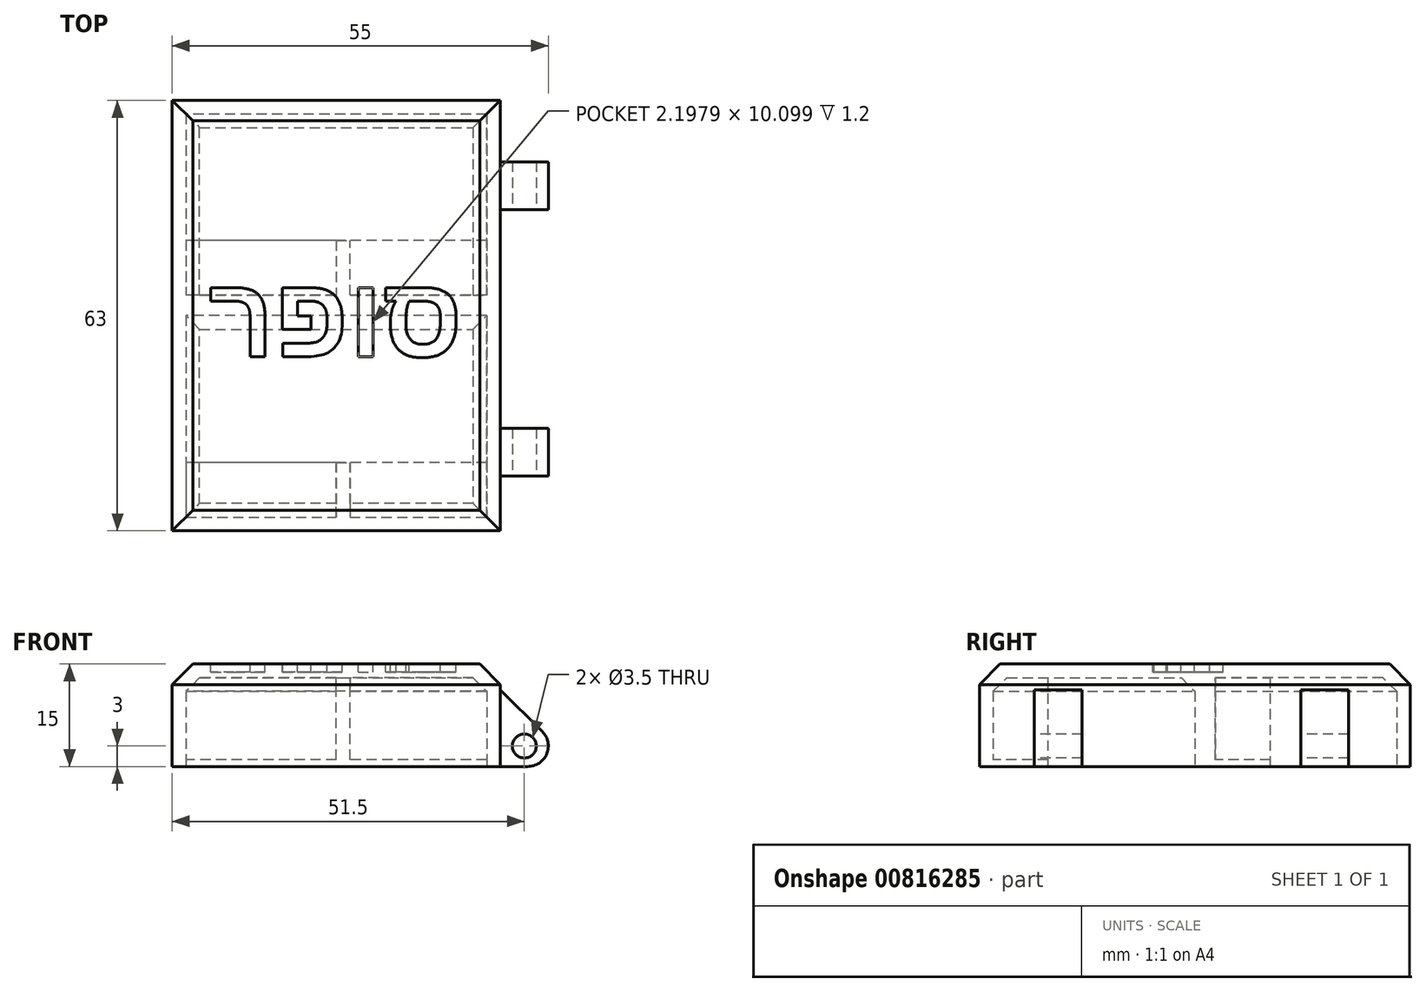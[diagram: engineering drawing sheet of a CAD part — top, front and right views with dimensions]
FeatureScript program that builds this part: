
annotation { "Feature Type Name" : "Feature", "Feature Type Description" : "" }
export const myFeature = defineFeature(function(context is Context, id is Id, definition is map)
    precondition{}
    {
        {
            var Q0;
            Q0=qCreatedBy(makeId("Top.planeOp"),FACE);
            var sketch = newSketch(context, id + "F0", { "sketchPlane" : qUnion([Q0])});
            skLineSegment(sketch, "E0.bottom", {"start": v(0, 0) * mm, "end": v(48, 0) * mm});
            skLineSegment(sketch, "E0.top", {"start": v(0, 63) * mm, "end": v(48, 63) * mm});
            skLineSegment(sketch, "E0.left", {"start": v(0, 0) * mm, "end": v(0, 63) * mm});
            skLineSegment(sketch, "E0.right", {"start": v(48, 0) * mm, "end": v(48, 63) * mm});
            skSolve(sketch);
        }
        {
            var Q0;
            Q0=makeQuery(id+"F0.imprint","IMPRINT",FACE,{"disambiguationData":[TD([[makeQuery(id+"F0.imprint","IMPRINT",EDGE,{"derivedFrom":sQuery(id+"F0.wireOp",EDGE,"E0.bottom")}),1.0]])]});
            extrude(context, id + "F1", {"entities" : qUnion([Q0]), "depth" : 15 * mm, "offsetDistance" : 25 * mm});
        }
        {
            var Q0;
            Q0=makeQuery(id+"F1.opExtrude","CAP_FACE",FACE,{"disambiguationData":[OSD([sQuery(id+"F0.wireOp",EDGE,"E0.bottom"),sQuery(id+"F0.wireOp",EDGE,"E0.top"),sQuery(id+"F0.wireOp",EDGE,"E0.left"),sQuery(id+"F0.wireOp",EDGE,"E0.right")])],"isStart":true});
            var sketch = newSketch(context, id + "F2", { "sketchPlane" : qUnion([Q0])});
            skLineSegment(sketch, "E1.bottom", {"start": v(46, -61) * mm, "end": v(2, -61) * mm});
            skLineSegment(sketch, "E1.top", {"start": v(46, -2) * mm, "end": v(2, -2) * mm});
            skLineSegment(sketch, "E1.left", {"start": v(46, -61) * mm, "end": v(46, -2) * mm});
            skLineSegment(sketch, "E1.right", {"start": v(2, -61) * mm, "end": v(2, -2) * mm});
            skSolve(sketch);
        }
        {
            var Q0;
            Q0 = qSketchRegion(id + "F2", true);
            extrude(context, id + "F3", {"entities" : qUnion([Q0]), "operationType" : NewBodyOperationType.REMOVE, "oppositeDirection" : true, "depth" : 13 * mm, "offsetDistance" : 25 * mm});
        }
        {
            var Q0;
            Q0=makeQuery(id+"F1.opExtrude","CAP_FACE",FACE,{"disambiguationData":[OSD([sQuery(id+"F0.wireOp",EDGE,"E0.bottom"),sQuery(id+"F0.wireOp",EDGE,"E0.top"),sQuery(id+"F0.wireOp",EDGE,"E0.left"),sQuery(id+"F0.wireOp",EDGE,"E0.right")])],"isStart":true});
            var sketch = newSketch(context, id + "F4", { "sketchPlane" : qUnion([Q0])});
            skLineSegment(sketch, "E2.bottom", {"start": v(48, -8) * mm, "end": v(55, -8) * mm});
            skLineSegment(sketch, "E2.top", {"start": v(48, -15) * mm, "end": v(55, -15) * mm});
            skLineSegment(sketch, "E2.left", {"start": v(48, -8) * mm, "end": v(48, -15) * mm});
            skLineSegment(sketch, "E2.right", {"start": v(55, -8) * mm, "end": v(55, -15) * mm});
            skLineSegment(sketch, "E3.bottom", {"start": v(48, -47) * mm, "end": v(55, -47) * mm});
            skLineSegment(sketch, "E3.top", {"start": v(48, -54) * mm, "end": v(55, -54) * mm});
            skLineSegment(sketch, "E3.left", {"start": v(48, -47) * mm, "end": v(48, -54) * mm});
            skLineSegment(sketch, "E3.right", {"start": v(55, -47) * mm, "end": v(55, -54) * mm});
            skSolve(sketch);
        }
        {
            var Q0;
            Q0=makeQuery(id+"F4.imprint","IMPRINT",FACE,{"disambiguationData":[TD([[makeQuery(id+"F4.imprint","IMPRINT",EDGE,{"derivedFrom":sQuery(id+"F4.wireOp",EDGE,"E2.bottom")}),-1.0]])]});
            var Q1;
            Q1=makeQuery(id+"F4.imprint","IMPRINT",FACE,{"disambiguationData":[TD([[makeQuery(id+"F4.imprint","IMPRINT",EDGE,{"derivedFrom":sQuery(id+"F4.wireOp",EDGE,"E3.bottom")}),-1.0]])]});
            extrude(context, id + "F5", {"entities" : qUnion([Q0, Q1]), "operationType" : NewBodyOperationType.ADD, "oppositeDirection" : true, "depth" : 6 * mm, "offsetDistance" : 25 * mm});
        }
        {
            var Q0;
            Q0=makeQuery(id+"F5.opExtrude","SWEPT_FACE",FACE,{"disambiguationData":[OSD([sQuery(id+"F4.wireOp",EDGE,"E2.bottom")])]});
            var sketch = newSketch(context, id + "F6", { "sketchPlane" : qUnion([Q0])});
            skLineSegment(sketch, "E4", {"start": v(48, 6) * mm, "end": v(55, 0) * mm, "construction": true});
            skCircle(sketch, "E5", {"center": v(51.5, 3) * mm, "radius": 1.75 * mm});
            skSolve(sketch);
        }
        {
            var Q0;
            Q0=makeQuery(id+"F6.imprint","IMPRINT",FACE,{"disambiguationData":[TD([[makeQuery(id+"F6.imprint","IMPRINT",EDGE,{"derivedFrom":sQuery(id+"F6.wireOp",EDGE,"E5")}),1.0]])]});
            extrude(context, id + "F7", {"entities" : qUnion([Q0]), "operationType" : NewBodyOperationType.REMOVE, "oppositeDirection" : true, "depth" : 60.8 * mm, "offsetDistance" : 25 * mm});
        }
        {
            var Q0;
            Q0=makeQuery(id+"F5.opExtrude","CAP_EDGE",EDGE,{"disambiguationData":[OSD([sQuery(id+"F4.wireOp",EDGE,"E2.right")])],"isStart":true});
            var Q1;
            Q1=makeQuery(id+"F5.opExtrude","CAP_EDGE",EDGE,{"disambiguationData":[OSD([sQuery(id+"F4.wireOp",EDGE,"E2.right")])],"isStart":false});
            var Q2;
            Q2=makeQuery(id+"F5.opExtrude","CAP_EDGE",EDGE,{"disambiguationData":[OSD([sQuery(id+"F4.wireOp",EDGE,"E3.right")])],"isStart":false});
            var Q3;
            Q3=makeQuery(id+"F5.opExtrude","CAP_EDGE",EDGE,{"disambiguationData":[OSD([sQuery(id+"F4.wireOp",EDGE,"E3.right")])],"isStart":true});
            fillet(context, id + "F8", {"entities" : qUnion([Q0, Q1, Q2, Q3]), "tangentPropagation" : true, "radius" : 3 * mm, "defaultsChanged" : false, "vertexSettings" : [], "allowEdgeOverflow" : false});
        }
        {
            var Q0;
            Q0=makeQuery(id+"F5.boolean.opBoolean","MERGE",FACE,{"derivedFrom":[makeQuery(id+"F1.opExtrude","CAP_FACE",FACE,{"disambiguationData":[OSD([sQuery(id+"F0.wireOp",EDGE,"E0.bottom"),sQuery(id+"F0.wireOp",EDGE,"E0.top"),sQuery(id+"F0.wireOp",EDGE,"E0.left"),sQuery(id+"F0.wireOp",EDGE,"E0.right")])],"isStart":true}),makeQuery(id+"F5.opExtrude","CAP_FACE",FACE,{"disambiguationData":[OSD([sQuery(id+"F4.wireOp",EDGE,"E2.bottom"),sQuery(id+"F4.wireOp",EDGE,"E2.top"),sQuery(id+"F4.wireOp",EDGE,"E2.left"),sQuery(id+"F4.wireOp",EDGE,"E2.right")])],"isStart":true}),makeQuery(id+"F5.opExtrude","CAP_FACE",FACE,{"disambiguationData":[OSD([sQuery(id+"F4.wireOp",EDGE,"E3.bottom"),sQuery(id+"F4.wireOp",EDGE,"E3.top"),sQuery(id+"F4.wireOp",EDGE,"E3.left"),sQuery(id+"F4.wireOp",EDGE,"E3.right")])],"isStart":true})]});
            var sketch = newSketch(context, id + "F9", { "sketchPlane" : qUnion([Q0])});
            skLineSegment(sketch, "E6.bottom", {"start": v(46, -34.5) * mm, "end": v(2, -34.5) * mm});
            skLineSegment(sketch, "E6.top", {"start": v(46, -31.5) * mm, "end": v(2, -31.5) * mm});
            skLineSegment(sketch, "E6.left", {"start": v(46, -34.5) * mm, "end": v(46, -31.5) * mm});
            skLineSegment(sketch, "E6.right", {"start": v(2, -34.5) * mm, "end": v(2, -31.5) * mm});
            skSolve(sketch);
        }
        {
            var Q0;
            Q0=makeQuery(id+"F9.imprint","IMPRINT",FACE,{"disambiguationData":[TD([[makeQuery(id+"F9.imprint","IMPRINT",EDGE,{"derivedFrom":sQuery(id+"F9.wireOp",EDGE,"E6.bottom")}),-1.0]])]});
            extrude(context, id + "F10", {"entities" : qUnion([Q0]), "operationType" : NewBodyOperationType.ADD, "endBound" : BoundingType.UP_TO_NEXT, "oppositeDirection" : true, "depth" : 25 * mm, "offsetDistance" : 25 * mm});
        }
        {
            var Q0;
            Q0=makeQuery(id+"F10.boolean.opBoolean","MERGE",FACE,{"derivedFrom":[makeQuery(id+"F5.boolean.opBoolean","MERGE",FACE,{"derivedFrom":[makeQuery(id+"F1.opExtrude","CAP_FACE",FACE,{"disambiguationData":[OSD([sQuery(id+"F0.wireOp",EDGE,"E0.bottom"),sQuery(id+"F0.wireOp",EDGE,"E0.top"),sQuery(id+"F0.wireOp",EDGE,"E0.left"),sQuery(id+"F0.wireOp",EDGE,"E0.right")])],"isStart":true}),makeQuery(id+"F5.opExtrude","CAP_FACE",FACE,{"disambiguationData":[OSD([sQuery(id+"F4.wireOp",EDGE,"E2.bottom"),sQuery(id+"F4.wireOp",EDGE,"E2.top"),sQuery(id+"F4.wireOp",EDGE,"E2.left"),sQuery(id+"F4.wireOp",EDGE,"E2.right")])],"isStart":true}),makeQuery(id+"F5.opExtrude","CAP_FACE",FACE,{"disambiguationData":[OSD([sQuery(id+"F4.wireOp",EDGE,"E3.bottom"),sQuery(id+"F4.wireOp",EDGE,"E3.top"),sQuery(id+"F4.wireOp",EDGE,"E3.left"),sQuery(id+"F4.wireOp",EDGE,"E3.right")])],"isStart":true})]}),makeQuery(id+"F10.opExtrude","CAP_FACE",FACE,{"disambiguationData":[OSD([sQuery(id+"F9.wireOp",EDGE,"E6.bottom"),sQuery(id+"F9.wireOp",EDGE,"E6.top"),sQuery(id+"F9.wireOp",EDGE,"E6.left"),sQuery(id+"F9.wireOp",EDGE,"E6.right")])],"isStart":true})]});
            var sketch = newSketch(context, id + "F11", { "sketchPlane" : qUnion([Q0])});
            skLineSegment(sketch, "E7.bottom", {"start": v(46, -34.5) * mm, "end": v(2, -34.5) * mm});
            skLineSegment(sketch, "E7.top", {"start": v(46, -42.5) * mm, "end": v(2, -42.5) * mm});
            skLineSegment(sketch, "E7.left", {"start": v(46, -34.5) * mm, "end": v(46, -42.5) * mm});
            skLineSegment(sketch, "E7.right", {"start": v(2, -34.5) * mm, "end": v(2, -42.5) * mm});
            skLineSegment(sketch, "E8.bottom", {"start": v(46, -2) * mm, "end": v(2, -2) * mm});
            skLineSegment(sketch, "E8.top", {"start": v(46, -10) * mm, "end": v(2, -10) * mm});
            skLineSegment(sketch, "E8.left", {"start": v(46, -2) * mm, "end": v(46, -10) * mm});
            skLineSegment(sketch, "E8.right", {"start": v(2, -2) * mm, "end": v(2, -10) * mm});
            skSolve(sketch);
        }
        {
            var Q0;
            Q0=makeQuery(id+"F11.imprint","IMPRINT",FACE,{"disambiguationData":[TD([[makeQuery(id+"F11.imprint","IMPRINT",EDGE,{"derivedFrom":sQuery(id+"F11.wireOp",EDGE,"E7.bottom")}),1.0]])]});
            var Q1;
            Q1=makeQuery(id+"F11.imprint","IMPRINT",FACE,{"disambiguationData":[TD([[makeQuery(id+"F11.imprint","IMPRINT",EDGE,{"derivedFrom":sQuery(id+"F11.wireOp",EDGE,"E8.bottom")}),1.0]])]});
            extrude(context, id + "F12", {"entities" : qUnion([Q0, Q1]), "operationType" : NewBodyOperationType.ADD, "oppositeDirection" : true, "depth" : 1 * mm, "offsetDistance" : 25 * mm});
        }
        {
            var Q0;
            Q0=makeQuery(id+"F12.boolean.opBoolean","MERGE",FACE,{"derivedFrom":[makeQuery(id+"F10.boolean.opBoolean","MERGE",FACE,{"derivedFrom":[makeQuery(id+"F5.boolean.opBoolean","MERGE",FACE,{"derivedFrom":[makeQuery(id+"F1.opExtrude","CAP_FACE",FACE,{"disambiguationData":[OSD([sQuery(id+"F0.wireOp",EDGE,"E0.bottom"),sQuery(id+"F0.wireOp",EDGE,"E0.top"),sQuery(id+"F0.wireOp",EDGE,"E0.left"),sQuery(id+"F0.wireOp",EDGE,"E0.right")])],"isStart":true}),makeQuery(id+"F5.opExtrude","CAP_FACE",FACE,{"disambiguationData":[OSD([sQuery(id+"F4.wireOp",EDGE,"E2.bottom"),sQuery(id+"F4.wireOp",EDGE,"E2.top"),sQuery(id+"F4.wireOp",EDGE,"E2.left"),sQuery(id+"F4.wireOp",EDGE,"E2.right")])],"isStart":true}),makeQuery(id+"F5.opExtrude","CAP_FACE",FACE,{"disambiguationData":[OSD([sQuery(id+"F4.wireOp",EDGE,"E3.bottom"),sQuery(id+"F4.wireOp",EDGE,"E3.top"),sQuery(id+"F4.wireOp",EDGE,"E3.left"),sQuery(id+"F4.wireOp",EDGE,"E3.right")])],"isStart":true})]}),makeQuery(id+"F10.opExtrude","CAP_FACE",FACE,{"disambiguationData":[OSD([sQuery(id+"F9.wireOp",EDGE,"E6.bottom"),sQuery(id+"F9.wireOp",EDGE,"E6.top"),sQuery(id+"F9.wireOp",EDGE,"E6.left"),sQuery(id+"F9.wireOp",EDGE,"E6.right")])],"isStart":true})]}),makeQuery(id+"F12.opExtrude","CAP_FACE",FACE,{"disambiguationData":[OSD([sQuery(id+"F11.wireOp",EDGE,"E7.bottom"),sQuery(id+"F11.wireOp",EDGE,"E7.top"),sQuery(id+"F11.wireOp",EDGE,"E7.left"),sQuery(id+"F11.wireOp",EDGE,"E7.right")])],"isStart":true}),makeQuery(id+"F12.opExtrude","CAP_FACE",FACE,{"disambiguationData":[OSD([sQuery(id+"F11.wireOp",EDGE,"E8.bottom"),sQuery(id+"F11.wireOp",EDGE,"E8.top"),sQuery(id+"F11.wireOp",EDGE,"E8.left"),sQuery(id+"F11.wireOp",EDGE,"E8.right")])],"isStart":true})]});
            var sketch = newSketch(context, id + "F13", { "sketchPlane" : qUnion([Q0])});
            skLineSegment(sketch, "E9.bottom", {"start": v(26, -42.5) * mm, "end": v(24, -42.5) * mm});
            skLineSegment(sketch, "E9.top", {"start": v(26, -31.5) * mm, "end": v(24, -31.5) * mm});
            skLineSegment(sketch, "E9.left", {"start": v(26, -42.5) * mm, "end": v(26, -31.5) * mm});
            skLineSegment(sketch, "E9.right", {"start": v(24, -42.5) * mm, "end": v(24, -31.5) * mm});
            skLineSegment(sketch, "E10.bottom", {"start": v(24, -10) * mm, "end": v(26, -10) * mm});
            skLineSegment(sketch, "E10.top", {"start": v(24, 0) * mm, "end": v(26, 0) * mm});
            skLineSegment(sketch, "E10.left", {"start": v(24, -10) * mm, "end": v(24, 0) * mm});
            skLineSegment(sketch, "E10.right", {"start": v(26, -10) * mm, "end": v(26, 0) * mm});
            skSolve(sketch);
        }
        {
            var Q0;
            Q0=makeQuery(id+"F13.imprint","IMPRINT",FACE,{"disambiguationData":[TD([[makeQuery(id+"F13.imprint","IMPRINT",EDGE,{"derivedFrom":sQuery(id+"F13.wireOp",EDGE,"E9.bottom")}),-1.0]])]});
            var Q1;
            Q1=makeQuery(id+"F13.imprint","IMPRINT",FACE,{"disambiguationData":[TD([[makeQuery(id+"F13.imprint","IMPRINT",EDGE,{"derivedFrom":sQuery(id+"F13.wireOp",EDGE,"E10.bottom")}),-1.0]])]});
            var Q2;
            {var subQ0=sQuery(id+"F2.wireOp",EDGE,"E1.bottom");var subQ1=sQuery(id+"F2.wireOp",EDGE,"E1.left");var subQ2=sQuery(id+"F2.wireOp",EDGE,"E1.right");Q2=makeQuery(id+"F10.boolean.opBoolean","SPLIT",FACE,{"disambiguationData":[TD([makeQuery(id+"F3.boolean.opBoolean","COPY",FACE,{"derivedFrom":makeQuery(id+"F3.opExtrude","SWEPT_FACE",FACE,{"disambiguationData":[OSD([subQ0])]})})])],"derivedFrom":makeQuery(id+"F3.boolean.opBoolean","COPY",FACE,{"derivedFrom":makeQuery(id+"F3.opExtrude","CAP_FACE",FACE,{"disambiguationData":[OSD([subQ0,sQuery(id+"F2.wireOp",EDGE,"E1.top"),subQ1,subQ2])],"isStart":false})})});}
            extrude(context, id + "F14", {"entities" : qUnion([Q0, Q1]), "operationType" : NewBodyOperationType.ADD, "endBound" : BoundingType.UP_TO_SURFACE, "oppositeDirection" : true, "depth" : 25 * mm, "endBoundEntityFace" : qUnion([Q2]), "offsetDistance" : 25 * mm});
        }
        {
            var Q0;
            Q0=makeQuery(id+"F1.opExtrude","CAP_EDGE",EDGE,{"disambiguationData":[OSD([sQuery(id+"F0.wireOp",EDGE,"E0.right")])],"isStart":false});
            var Q1;
            Q1=makeQuery(id+"F1.opExtrude","CAP_EDGE",EDGE,{"disambiguationData":[OSD([sQuery(id+"F0.wireOp",EDGE,"E0.bottom")])],"isStart":false});
            var Q2;
            Q2=makeQuery(id+"F1.opExtrude","CAP_EDGE",EDGE,{"disambiguationData":[OSD([sQuery(id+"F0.wireOp",EDGE,"E0.left")])],"isStart":false});
            var Q3;
            Q3=makeQuery(id+"F1.opExtrude","CAP_EDGE",EDGE,{"disambiguationData":[OSD([sQuery(id+"F0.wireOp",EDGE,"E0.top")])],"isStart":false});
            chamfer(context, id + "F15", {"entities" : qUnion([Q0, Q1, Q2, Q3]), "width" : 3 * mm, "tangentPropagation" : true});
        }
        {
            var Q0;
            Q0=makeQuery(id+"F3.boolean.opBoolean","COPY",EDGE,{"derivedFrom":makeQuery(id+"F3.opExtrude","CAP_EDGE",EDGE,{"disambiguationData":[OSD([sQuery(id+"F2.wireOp",EDGE,"E1.bottom")])],"isStart":false})});
            var Q1;
            Q1=makeQuery(id+"F3.boolean.opBoolean","COPY",EDGE,{"derivedFrom":makeQuery(id+"F3.opExtrude","CAP_EDGE",EDGE,{"disambiguationData":[OSD([sQuery(id+"F2.wireOp",EDGE,"E1.left")])],"isStart":false})});
            var Q2;
            Q2=makeQuery(id+"F3.boolean.opBoolean","COPY",EDGE,{"derivedFrom":makeQuery(id+"F3.opExtrude","CAP_EDGE",EDGE,{"disambiguationData":[OSD([sQuery(id+"F2.wireOp",EDGE,"E1.top")])],"isStart":false})});
            var Q3;
            Q3=makeQuery(id+"F3.boolean.opBoolean","COPY",EDGE,{"derivedFrom":makeQuery(id+"F3.opExtrude","CAP_EDGE",EDGE,{"disambiguationData":[OSD([sQuery(id+"F2.wireOp",EDGE,"E1.right")])],"isStart":false})});
            var Q4;
            Q4=makeQuery(id+"F10.opExtrude","CAP_EDGE",EDGE,{"disambiguationData":[OSD([sQuery(id+"F9.wireOp",EDGE,"E6.top")])],"isStart":false});
            var Q5;
            Q5=makeQuery(id+"F10.opExtrude","CAP_EDGE",EDGE,{"disambiguationData":[OSD([sQuery(id+"F9.wireOp",EDGE,"E6.bottom")])],"isStart":false});
            chamfer(context, id + "F16", {"entities" : qUnion([Q0, Q1, Q2, Q3, Q4, Q5]), "width" : 2 * mm, "tangentPropagation" : true});
        }
        {
            var Q0;
            Q0=makeQuery(id+"F5.opExtrude","SWEPT_FACE",FACE,{"disambiguationData":[OSD([sQuery(id+"F4.wireOp",EDGE,"E2.bottom")])]});
            var sketch = newSketch(context, id + "F17", { "sketchPlane" : qUnion([Q0])});
            skLineSegment(sketch, "E11", {"start": v(48, 6) * mm, "end": v(48, 11.24) * mm});
            skLineSegment(sketch, "E12", {"start": v(48, 11.24) * mm, "end": v(54.12, 5.12) * mm});
            skArc(sketch, "E13.0", {"start": v(54.12, 5.12) * mm, "mid": v(53.15, 5.77) * mm, "end": v(52, 6) * mm});
            skLineSegment(sketch, "E13.1", {"start": v(48, 6) * mm, "end": v(52, 6) * mm});
            skPoint(sketch, "E14.orphan", {"position": v(52, 0) * mm});
            skSolve(sketch);
        }
        {
            var Q0;
            Q0=makeQuery(id+"F17.imprint","IMPRINT",FACE,{"disambiguationData":[TD([[makeQuery(id+"F17.imprint","IMPRINT",EDGE,{"derivedFrom":sQuery(id+"F17.wireOp",EDGE,"E11")}),-1.0]])]});
            var Q1;
            Q1=makeQuery(id+"F5.opExtrude","SWEPT_FACE",FACE,{"disambiguationData":[OSD([sQuery(id+"F4.wireOp",EDGE,"E2.top")])]});
            extrude(context, id + "F18", {"entities" : qUnion([Q0]), "operationType" : NewBodyOperationType.ADD, "endBound" : BoundingType.UP_TO_SURFACE, "oppositeDirection" : true, "depth" : 25 * mm, "endBoundEntityFace" : qUnion([Q1]), "offsetDistance" : 25 * mm});
        }
        {
            var Q0;
            Q0=makeQuery(id+"F5.opExtrude","SWEPT_FACE",FACE,{"disambiguationData":[OSD([sQuery(id+"F4.wireOp",EDGE,"E3.bottom")])]});
            var sketch = newSketch(context, id + "F19", { "sketchPlane" : qUnion([Q0])});
            skLineSegment(sketch, "E15", {"start": v(48, 6) * mm, "end": v(48, 11.24) * mm});
            skLineSegment(sketch, "E16", {"start": v(48, 11.24) * mm, "end": v(54.12, 5.12) * mm});
            skLineSegment(sketch, "E17.0", {"start": v(48, 6) * mm, "end": v(52, 6) * mm});
            skArc(sketch, "E17.1", {"start": v(54.12, 5.12) * mm, "mid": v(53.15, 5.77) * mm, "end": v(52, 6) * mm});
            skPoint(sketch, "E18.orphan", {"position": v(52, 0) * mm});
            skSolve(sketch);
        }
        {
            var Q0;
            Q0=makeQuery(id+"F19.imprint","IMPRINT",FACE,{"disambiguationData":[TD([[makeQuery(id+"F19.imprint","IMPRINT",EDGE,{"derivedFrom":sQuery(id+"F19.wireOp",EDGE,"E15")}),-1.0]])]});
            var Q1;
            Q1=makeQuery(id+"F5.opExtrude","SWEPT_FACE",FACE,{"disambiguationData":[OSD([sQuery(id+"F4.wireOp",EDGE,"E3.top")])]});
            extrude(context, id + "F20", {"entities" : qUnion([Q0]), "operationType" : NewBodyOperationType.ADD, "endBound" : BoundingType.UP_TO_SURFACE, "oppositeDirection" : true, "depth" : 25 * mm, "endBoundEntityFace" : qUnion([Q1]), "offsetDistance" : 25 * mm});
        }
        {
            var Q0;
            Q0=makeQuery(id+"F1.opExtrude","CAP_FACE",FACE,{"disambiguationData":[OSD([sQuery(id+"F0.wireOp",EDGE,"E0.bottom"),sQuery(id+"F0.wireOp",EDGE,"E0.top"),sQuery(id+"F0.wireOp",EDGE,"E0.left"),sQuery(id+"F0.wireOp",EDGE,"E0.right")])],"isStart":false});
            var sketch = newSketch(context, id + "F21", { "sketchPlane" : qUnion([Q0])});
            skText(sketch, "E19", { "text": "רפוס", "fontName": "Arimo-Bold.ttf"});
            skLineSegment(sketch, "E20", {"start": v(24, 37.5) * mm, "end": v(24, 60) * mm});
            skLineSegment(sketch, "E21", {"start": v(24, 3) * mm, "end": v(24, 25.5) * mm});
            skLineSegment(sketch, "E22", {"start": v(3, 31.5) * mm, "end": v(5.31, 31.5) * mm});
            skLineSegment(sketch, "E23", {"start": v(42.69, 31.5) * mm, "end": v(45, 31.5) * mm});
            skLineSegment(sketch, "E24", {"start": v(45, 31.5) * mm, "end": v(43.84, 31.5) * mm});
            const initialGuessF21  = {"E19": [0.00531, 0.0255, 1, 0, 0.012]};
            skSetInitialGuess(sketch, initialGuessF21);
            skSolve(sketch);
        }
        {
            var Q0;
            Q0 = qSketchRegion(id + "F21", true);
            extrude(context, id + "F22", {"entities" : qUnion([Q0]), "operationType" : NewBodyOperationType.REMOVE, "oppositeDirection" : true, "depth" : 1.2 * mm, "offsetDistance" : 25 * mm});
        }
    });
